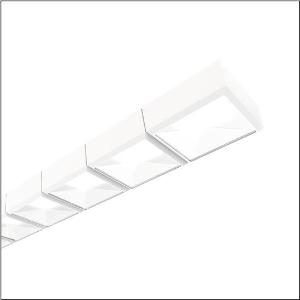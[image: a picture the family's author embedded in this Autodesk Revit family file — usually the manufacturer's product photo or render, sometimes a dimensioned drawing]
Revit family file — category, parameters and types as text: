
# Revit family: scriptus_r__11_5mz314d0twb_59a6
name_source: partatom
category: Lighting Fixtures
units: mm (PartAtom-declared; Revit-internal decimal feet)

## family parameters
Cut with Voids When Loaded = No
Host = Face
Light Source = No
Part Type = Normal
Room Calculation Point = No
Round Connector Dimension = Use Diameter
Shared = No

## types (1)
- --- (1 x LED 3000K+6500K / CRI = 80 (unbekannt), 3390 lm / 3600 lm, 3000K)
    Apparent Load = 106 VA
    CIE Flux Codes = 0 0 0 0 100 / 82 95 99 100 100
    Color Rendering = 80
    Color Temperature = 3000K
    Default Elevation = 1800 mm
    Description = Scriptus® 11, office luminaire, primary optical cover: lenses, CAT 2 (L<= 3000cd/m²), light emission: direct/indirect distribution, primary light characteristic: symmetric, installation type: suspended mounting, LED, rated luminous flux: 13.970lm, luminous efficacy: 128lm/W, light colour: 8tw, colour temperature: 3000..6500K, control gear: ECG DALI, with terminal, 5-pole, mains connection: 230V, AC, 50Hz, rated input power: 110W, LED, control gear: ECG DALI, housing, luminaire housing, of aluminium, traffic white (RAL 9016), length: 3.088mm, width: 114mm, height: 57mm, protection rating (complete): IP20, insulation class (complete): insulation class I (protective earthing), certification: CE, protection symbol: F, permissible operating ambient temperature: <= +25°C, standard: EN 50419, packaging unit: 1 piece
    Height = 57 mm
    Lamp = 1 x LED 3000K+6500K / CRI >= 80 (unbekannt)
    Lamp Light Flux = 3390 lm / 3600 lm
    Lamp count = 1
    Length = 3088 mm
    Luminous efficacy = 132 lm/W
    Manufacturer = Siteco
    ModVariant = No
    Model = 5MZ314D0TWB
    Mounting Place = Ceiling
    Mounting Type = Pendant
    Number of Poles = 1
    OnlyDefault = Yes
    Power Factor = 1
    Product Name = Scriptus® 11
    Product group = office luminaire | ceiling pendant
    ProductGroupID = 902
    Protection Class = Protection class I
    Protection Degree = IP 20
    RLX_Detail_Level = 1
    RLX_Emergency_Light_Flux = 0 lm
    RLX_Emergency_Type = 0
    RLX_Emergency_Type_DB = No
    RlxData = <blob elided: 32273 chars, md5=f2915556>
    Socket = socket
    Standby Power = 0 W
    System Light Flux = 13980 lm
    System Power = 106 W
    Type Comments = individual setting: colour temperature 6500K
    Type Image = l_1004839.jpg
    URL = http://relux.com
    VarID = @adj_148940
    Voltage = 0 V
    Weight = 0.00 kg
    Width = 114 mm

## geometry (parser evidence)
native form markers: Blend x4, Sweep x20
no freeform markers — native parametric forms only
